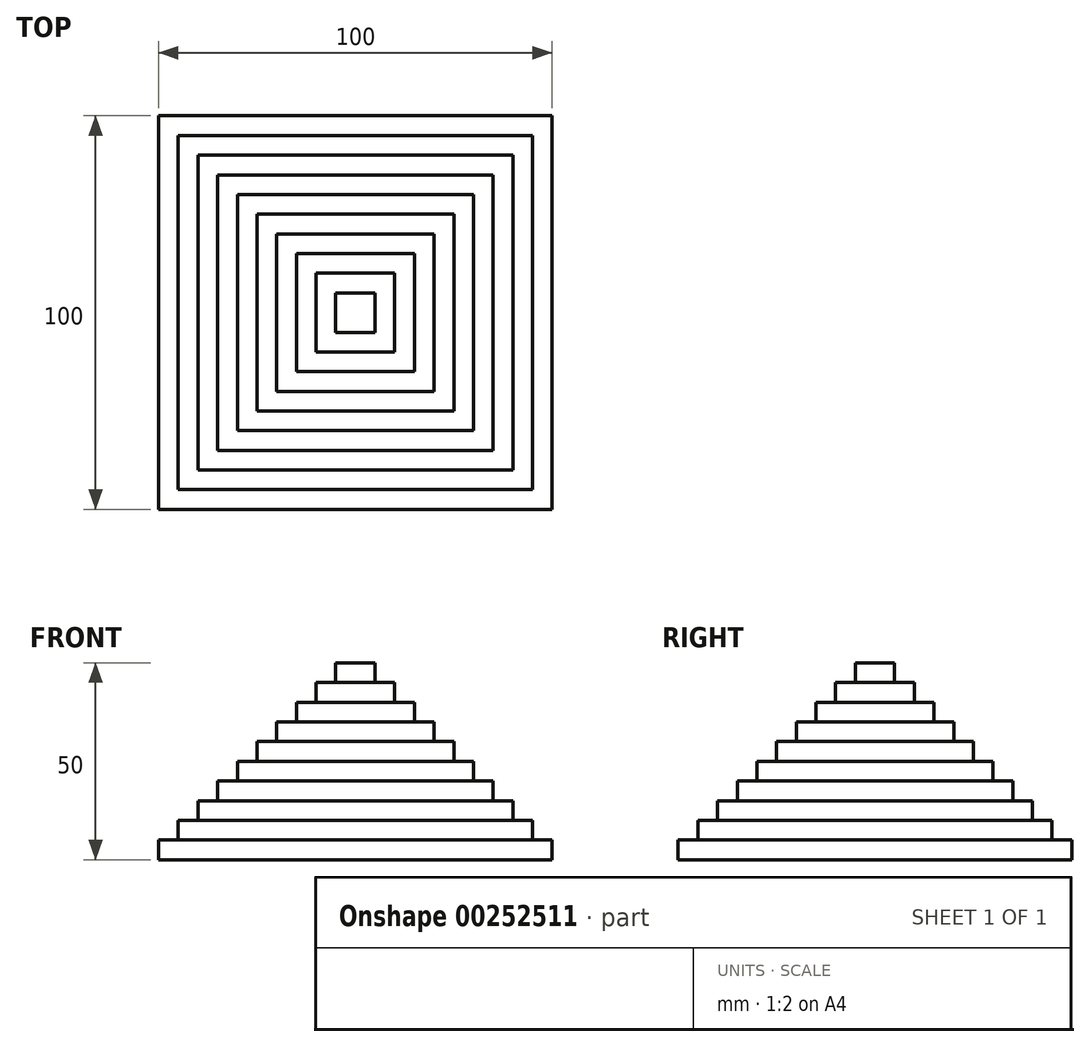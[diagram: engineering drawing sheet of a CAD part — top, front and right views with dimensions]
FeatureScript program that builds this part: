
annotation { "Feature Type Name" : "Feature", "Feature Type Description" : "" }
export const myFeature = defineFeature(function(context is Context, id is Id, definition is map)
    precondition{}
    {
        {
            var Q0;
            Q0=qCreatedBy(makeId("Top.planeOp"),FACE);
            var sketch = newSketch(context, id + "F0", { "sketchPlane" : qUnion([Q0])});
            skLineSegment(sketch, "E0.bottom", {"start": v(50, -50) * mm, "end": v(-50, -50) * mm});
            skLineSegment(sketch, "E0.top", {"start": v(50, 50) * mm, "end": v(-50, 50) * mm});
            skLineSegment(sketch, "E0.left", {"start": v(50, -50) * mm, "end": v(50, 50) * mm});
            skLineSegment(sketch, "E0.right", {"start": v(-50, -50) * mm, "end": v(-50, 50) * mm});
            skPoint(sketch, "E0.middle", {"position": v(0, 0) * mm});
            skSolve(sketch);
        }
        {
            var Q0;
            Q0 = qSketchRegion(id + "F0", true);
            extrude(context, id + "F1", {"entities" : qUnion([Q0]), "depth" : 5 * mm});
        }
        {
            var Q0;
            Q0=makeQuery(id+"F1.opExtrude","CAP_FACE",FACE,{"disambiguationData":[OSD([sQuery(id+"F0.wireOp",EDGE,"E0.bottom"),sQuery(id+"F0.wireOp",EDGE,"E0.top"),sQuery(id+"F0.wireOp",EDGE,"E0.left"),sQuery(id+"F0.wireOp",EDGE,"E0.right")])],"isStart":false});
            var sketch = newSketch(context, id + "F2", { "sketchPlane" : qUnion([Q0])});
            skLineSegment(sketch, "E1.bottom", {"start": v(47.5, -47.5) * mm, "end": v(-47.5, -47.5) * mm});
            skLineSegment(sketch, "E1.top", {"start": v(47.5, 47.5) * mm, "end": v(-47.5, 47.5) * mm});
            skLineSegment(sketch, "E1.left", {"start": v(47.5, -47.5) * mm, "end": v(47.5, 47.5) * mm});
            skLineSegment(sketch, "E1.right", {"start": v(-47.5, -47.5) * mm, "end": v(-47.5, 47.5) * mm});
            skPoint(sketch, "E1.middle", {"position": v(0, 0) * mm});
            skSolve(sketch);
        }
        {
            var Q0;
            Q0=makeQuery(id+"F2.imprint","IMPRINT",FACE,{"disambiguationData":[TD([[makeQuery(id+"F2.imprint","IMPRINT",EDGE,{"derivedFrom":sQuery(id+"F2.wireOp",EDGE,"E1.bottom")}),-1.0]])]});
            extrude(context, id + "F3", {"entities" : qUnion([Q0]), "operationType" : NewBodyOperationType.REMOVE, "oppositeDirection" : true, "depth" : 3 * mm});
        }
        {
            var Q0;
            Q0=makeQuery(id+"F3.boolean.opBoolean","COPY",FACE,{"derivedFrom":makeQuery(id+"F3.opExtrude","CAP_FACE",FACE,{"disambiguationData":[OSD([sQuery(id+"F2.wireOp",EDGE,"E1.bottom"),sQuery(id+"F2.wireOp",EDGE,"E1.top"),sQuery(id+"F2.wireOp",EDGE,"E1.left"),sQuery(id+"F2.wireOp",EDGE,"E1.right")])],"isStart":false})});
            var sketch = newSketch(context, id + "F4", { "sketchPlane" : qUnion([Q0])});
            skLineSegment(sketch, "E2.bottom", {"start": v(47.5, -47.5) * mm, "end": v(-47.5, -47.5) * mm});
            skLineSegment(sketch, "E2.top", {"start": v(47.5, 47.5) * mm, "end": v(-47.5, 47.5) * mm});
            skLineSegment(sketch, "E2.left", {"start": v(47.5, -47.5) * mm, "end": v(47.5, 47.5) * mm});
            skLineSegment(sketch, "E2.right", {"start": v(-47.5, -47.5) * mm, "end": v(-47.5, 47.5) * mm});
            skPoint(sketch, "E2.middle", {"position": v(0, 0) * mm});
            skSolve(sketch);
        }
        {
            var Q0;
            Q0 = qSketchRegion(id + "F4", true);
            extrude(context, id + "F5", {"entities" : qUnion([Q0]), "depth" : 2 * mm});
        }
        {
            var Q0;
            Q0=makeQuery(id+"F5.opExtrude","CAP_FACE",FACE,{"disambiguationData":[OSD([sQuery(id+"F4.wireOp",EDGE,"E2.bottom"),sQuery(id+"F4.wireOp",EDGE,"E2.top"),sQuery(id+"F4.wireOp",EDGE,"E2.left"),sQuery(id+"F4.wireOp",EDGE,"E2.right")])],"isStart":false});
            var sketch = newSketch(context, id + "F6", { "sketchPlane" : qUnion([Q0])});
            skLineSegment(sketch, "E3.bottom", {"start": v(47.5, -47.5) * mm, "end": v(-47.5, -47.5) * mm});
            skLineSegment(sketch, "E3.top", {"start": v(47.5, 47.5) * mm, "end": v(-47.5, 47.5) * mm});
            skLineSegment(sketch, "E3.left", {"start": v(47.5, -47.5) * mm, "end": v(47.5, 47.5) * mm});
            skLineSegment(sketch, "E3.right", {"start": v(-47.5, -47.5) * mm, "end": v(-47.5, 47.5) * mm});
            skPoint(sketch, "E3.middle", {"position": v(0, 0) * mm});
            skSolve(sketch);
        }
        {
            var Q0;
            Q0 = qSketchRegion(id + "F6", true);
            extrude(context, id + "F7", {"entities" : qUnion([Q0]), "operationType" : NewBodyOperationType.ADD, "depth" : 1 * mm});
        }
        {
            var Q0;
            Q0=makeQuery(id+"F7.boolean.opBoolean","MERGE",FACE,{"derivedFrom":[makeQuery(id+"F1.opExtrude","CAP_FACE",FACE,{"disambiguationData":[OSD([sQuery(id+"F0.wireOp",EDGE,"E0.bottom"),sQuery(id+"F0.wireOp",EDGE,"E0.top"),sQuery(id+"F0.wireOp",EDGE,"E0.left"),sQuery(id+"F0.wireOp",EDGE,"E0.right")])],"isStart":false}),makeQuery(id+"F7.opExtrude","CAP_FACE",FACE,{"disambiguationData":[OSD([sQuery(id+"F6.wireOp",EDGE,"E3.bottom"),sQuery(id+"F6.wireOp",EDGE,"E3.top"),sQuery(id+"F6.wireOp",EDGE,"E3.left"),sQuery(id+"F6.wireOp",EDGE,"E3.right")])],"isStart":false})]});
            var sketch = newSketch(context, id + "F8", { "sketchPlane" : qUnion([Q0])});
            skLineSegment(sketch, "E4.bottom", {"start": v(45, -45) * mm, "end": v(-45, -45) * mm});
            skLineSegment(sketch, "E4.top", {"start": v(45, 45) * mm, "end": v(-45, 45) * mm});
            skLineSegment(sketch, "E4.left", {"start": v(45, -45) * mm, "end": v(45, 45) * mm});
            skLineSegment(sketch, "E4.right", {"start": v(-45, -45) * mm, "end": v(-45, 45) * mm});
            skPoint(sketch, "E4.middle", {"position": v(0, 0) * mm});
            skSolve(sketch);
        }
        {
            var Q0;
            Q0 = qSketchRegion(id + "F8", true);
            extrude(context, id + "F9", {"entities" : qUnion([Q0]), "operationType" : NewBodyOperationType.ADD, "depth" : 5 * mm});
        }
        {
            var Q0;
            Q0=makeQuery(id+"F9.opExtrude","CAP_FACE",FACE,{"disambiguationData":[OSD([sQuery(id+"F8.wireOp",EDGE,"E4.bottom"),sQuery(id+"F8.wireOp",EDGE,"E4.top"),sQuery(id+"F8.wireOp",EDGE,"E4.left"),sQuery(id+"F8.wireOp",EDGE,"E4.right")])],"isStart":false});
            var sketch = newSketch(context, id + "F10", { "sketchPlane" : qUnion([Q0])});
            skLineSegment(sketch, "E5.bottom", {"start": v(42.5, -42.5) * mm, "end": v(-42.5, -42.5) * mm});
            skLineSegment(sketch, "E5.top", {"start": v(42.5, 42.5) * mm, "end": v(-42.5, 42.5) * mm});
            skLineSegment(sketch, "E5.left", {"start": v(42.5, -42.5) * mm, "end": v(42.5, 42.5) * mm});
            skLineSegment(sketch, "E5.right", {"start": v(-42.5, -42.5) * mm, "end": v(-42.5, 42.5) * mm});
            skPoint(sketch, "E5.middle", {"position": v(0, 0) * mm});
            skSolve(sketch);
        }
        {
            var Q0;
            Q0 = qSketchRegion(id + "F10", true);
            extrude(context, id + "F11", {"entities" : qUnion([Q0]), "operationType" : NewBodyOperationType.REMOVE, "oppositeDirection" : true, "depth" : 3 * mm});
        }
        {
            var Q0;
            Q0=makeQuery(id+"F11.boolean.opBoolean","COPY",FACE,{"derivedFrom":makeQuery(id+"F11.opExtrude","CAP_FACE",FACE,{"disambiguationData":[OSD([sQuery(id+"F10.wireOp",EDGE,"E5.bottom"),sQuery(id+"F10.wireOp",EDGE,"E5.top"),sQuery(id+"F10.wireOp",EDGE,"E5.left"),sQuery(id+"F10.wireOp",EDGE,"E5.right")])],"isStart":false})});
            var sketch = newSketch(context, id + "F12", { "sketchPlane" : qUnion([Q0])});
            skLineSegment(sketch, "E6.bottom", {"start": v(42.5, -42.5) * mm, "end": v(-42.5, -42.5) * mm});
            skLineSegment(sketch, "E6.top", {"start": v(42.5, 42.5) * mm, "end": v(-42.5, 42.5) * mm});
            skLineSegment(sketch, "E6.left", {"start": v(42.5, -42.5) * mm, "end": v(42.5, 42.5) * mm});
            skLineSegment(sketch, "E6.right", {"start": v(-42.5, -42.5) * mm, "end": v(-42.5, 42.5) * mm});
            skPoint(sketch, "E6.middle", {"position": v(0, 0) * mm});
            skSolve(sketch);
        }
        {
            var Q0;
            Q0 = qSketchRegion(id + "F12", true);
            extrude(context, id + "F13", {"entities" : qUnion([Q0]), "depth" : 2 * mm});
        }
        {
            var Q0;
            Q0=makeQuery(id+"F13.opExtrude","CAP_FACE",FACE,{"disambiguationData":[OSD([sQuery(id+"F12.wireOp",EDGE,"E6.bottom"),sQuery(id+"F12.wireOp",EDGE,"E6.top"),sQuery(id+"F12.wireOp",EDGE,"E6.left"),sQuery(id+"F12.wireOp",EDGE,"E6.right")])],"isStart":false});
            var sketch = newSketch(context, id + "F14", { "sketchPlane" : qUnion([Q0])});
            skLineSegment(sketch, "E7.bottom", {"start": v(42.5, -42.5) * mm, "end": v(-42.5, -42.5) * mm});
            skLineSegment(sketch, "E7.top", {"start": v(42.5, 42.5) * mm, "end": v(-42.5, 42.5) * mm});
            skLineSegment(sketch, "E7.left", {"start": v(42.5, -42.5) * mm, "end": v(42.5, 42.5) * mm});
            skLineSegment(sketch, "E7.right", {"start": v(-42.5, -42.5) * mm, "end": v(-42.5, 42.5) * mm});
            skPoint(sketch, "E7.middle", {"position": v(0, 0) * mm});
            skSolve(sketch);
        }
        {
            var Q0;
            Q0 = qSketchRegion(id + "F14", true);
            extrude(context, id + "F15", {"entities" : qUnion([Q0]), "operationType" : NewBodyOperationType.ADD, "depth" : 1 * mm});
        }
        {
            var Q0;
            Q0=makeQuery(id+"F15.boolean.opBoolean","MERGE",FACE,{"derivedFrom":[makeQuery(id+"F9.opExtrude","CAP_FACE",FACE,{"disambiguationData":[OSD([sQuery(id+"F8.wireOp",EDGE,"E4.bottom"),sQuery(id+"F8.wireOp",EDGE,"E4.top"),sQuery(id+"F8.wireOp",EDGE,"E4.left"),sQuery(id+"F8.wireOp",EDGE,"E4.right")])],"isStart":false}),makeQuery(id+"F15.opExtrude","CAP_FACE",FACE,{"disambiguationData":[OSD([sQuery(id+"F14.wireOp",EDGE,"E7.bottom"),sQuery(id+"F14.wireOp",EDGE,"E7.top"),sQuery(id+"F14.wireOp",EDGE,"E7.left"),sQuery(id+"F14.wireOp",EDGE,"E7.right")])],"isStart":false})]});
            var sketch = newSketch(context, id + "F16", { "sketchPlane" : qUnion([Q0])});
            skLineSegment(sketch, "E8.bottom", {"start": v(40, -40) * mm, "end": v(-40, -40) * mm});
            skLineSegment(sketch, "E8.top", {"start": v(40, 40) * mm, "end": v(-40, 40) * mm});
            skLineSegment(sketch, "E8.left", {"start": v(40, -40) * mm, "end": v(40, 40) * mm});
            skLineSegment(sketch, "E8.right", {"start": v(-40, -40) * mm, "end": v(-40, 40) * mm});
            skPoint(sketch, "E8.middle", {"position": v(0, 0) * mm});
            skSolve(sketch);
        }
        {
            var Q0;
            Q0 = qSketchRegion(id + "F16", true);
            extrude(context, id + "F17", {"entities" : qUnion([Q0]), "operationType" : NewBodyOperationType.ADD, "depth" : 5 * mm});
        }
        {
            var Q0;
            Q0=makeQuery(id+"F17.opExtrude","CAP_FACE",FACE,{"disambiguationData":[OSD([sQuery(id+"F16.wireOp",EDGE,"E8.bottom"),sQuery(id+"F16.wireOp",EDGE,"E8.top"),sQuery(id+"F16.wireOp",EDGE,"E8.left"),sQuery(id+"F16.wireOp",EDGE,"E8.right")])],"isStart":false});
            var sketch = newSketch(context, id + "F18", { "sketchPlane" : qUnion([Q0])});
            skLineSegment(sketch, "E9.bottom", {"start": v(37.5, -37.5) * mm, "end": v(-37.5, -37.5) * mm});
            skLineSegment(sketch, "E9.top", {"start": v(37.5, 37.5) * mm, "end": v(-37.5, 37.5) * mm});
            skLineSegment(sketch, "E9.left", {"start": v(37.5, -37.5) * mm, "end": v(37.5, 37.5) * mm});
            skLineSegment(sketch, "E9.right", {"start": v(-37.5, -37.5) * mm, "end": v(-37.5, 37.5) * mm});
            skPoint(sketch, "E9.middle", {"position": v(0, 0) * mm});
            skSolve(sketch);
        }
        {
            var Q0;
            Q0 = qSketchRegion(id + "F18", true);
            extrude(context, id + "F19", {"entities" : qUnion([Q0]), "operationType" : NewBodyOperationType.REMOVE, "oppositeDirection" : true, "depth" : 3 * mm});
        }
        {
            var Q0;
            Q0=makeQuery(id+"F19.boolean.opBoolean","COPY",FACE,{"derivedFrom":makeQuery(id+"F19.opExtrude","CAP_FACE",FACE,{"disambiguationData":[OSD([sQuery(id+"F18.wireOp",EDGE,"E9.bottom"),sQuery(id+"F18.wireOp",EDGE,"E9.top"),sQuery(id+"F18.wireOp",EDGE,"E9.left"),sQuery(id+"F18.wireOp",EDGE,"E9.right")])],"isStart":false})});
            var sketch = newSketch(context, id + "F20", { "sketchPlane" : qUnion([Q0])});
            skLineSegment(sketch, "E10.bottom", {"start": v(37.5, -37.5) * mm, "end": v(-37.5, -37.5) * mm});
            skLineSegment(sketch, "E10.top", {"start": v(37.5, 37.5) * mm, "end": v(-37.5, 37.5) * mm});
            skLineSegment(sketch, "E10.left", {"start": v(37.5, -37.5) * mm, "end": v(37.5, 37.5) * mm});
            skLineSegment(sketch, "E10.right", {"start": v(-37.5, -37.5) * mm, "end": v(-37.5, 37.5) * mm});
            skPoint(sketch, "E10.middle", {"position": v(0, 0) * mm});
            skSolve(sketch);
        }
        {
            var Q0;
            Q0 = qSketchRegion(id + "F20", true);
            extrude(context, id + "F21", {"entities" : qUnion([Q0]), "depth" : 2 * mm});
        }
        {
            var Q0;
            Q0=makeQuery(id+"F21.opExtrude","CAP_FACE",FACE,{"disambiguationData":[OSD([sQuery(id+"F20.wireOp",EDGE,"E10.bottom"),sQuery(id+"F20.wireOp",EDGE,"E10.top"),sQuery(id+"F20.wireOp",EDGE,"E10.left"),sQuery(id+"F20.wireOp",EDGE,"E10.right")])],"isStart":false});
            var sketch = newSketch(context, id + "F22", { "sketchPlane" : qUnion([Q0])});
            skLineSegment(sketch, "E11.bottom", {"start": v(37.5, -37.5) * mm, "end": v(-37.5, -37.5) * mm});
            skLineSegment(sketch, "E11.top", {"start": v(37.5, 37.5) * mm, "end": v(-37.5, 37.5) * mm});
            skLineSegment(sketch, "E11.left", {"start": v(37.5, -37.5) * mm, "end": v(37.5, 37.5) * mm});
            skLineSegment(sketch, "E11.right", {"start": v(-37.5, -37.5) * mm, "end": v(-37.5, 37.5) * mm});
            skPoint(sketch, "E11.middle", {"position": v(0, 0) * mm});
            skSolve(sketch);
        }
        {
            var Q0;
            Q0 = qSketchRegion(id + "F22", true);
            extrude(context, id + "F23", {"entities" : qUnion([Q0]), "operationType" : NewBodyOperationType.ADD, "depth" : 1 * mm});
        }
        {
            var Q0;
            Q0=makeQuery(id+"F23.boolean.opBoolean","MERGE",FACE,{"derivedFrom":[makeQuery(id+"F17.opExtrude","CAP_FACE",FACE,{"disambiguationData":[OSD([sQuery(id+"F16.wireOp",EDGE,"E8.bottom"),sQuery(id+"F16.wireOp",EDGE,"E8.top"),sQuery(id+"F16.wireOp",EDGE,"E8.left"),sQuery(id+"F16.wireOp",EDGE,"E8.right")])],"isStart":false}),makeQuery(id+"F23.opExtrude","CAP_FACE",FACE,{"disambiguationData":[OSD([sQuery(id+"F22.wireOp",EDGE,"E11.bottom"),sQuery(id+"F22.wireOp",EDGE,"E11.top"),sQuery(id+"F22.wireOp",EDGE,"E11.left"),sQuery(id+"F22.wireOp",EDGE,"E11.right")])],"isStart":false})]});
            var sketch = newSketch(context, id + "F24", { "sketchPlane" : qUnion([Q0])});
            skLineSegment(sketch, "E12.bottom", {"start": v(35, -35) * mm, "end": v(-35, -35) * mm});
            skLineSegment(sketch, "E12.top", {"start": v(35, 35) * mm, "end": v(-35, 35) * mm});
            skLineSegment(sketch, "E12.left", {"start": v(35, -35) * mm, "end": v(35, 35) * mm});
            skLineSegment(sketch, "E12.right", {"start": v(-35, -35) * mm, "end": v(-35, 35) * mm});
            skPoint(sketch, "E12.middle", {"position": v(0, 0) * mm});
            skSolve(sketch);
        }
        {
            var Q0;
            Q0=makeQuery(id+"F24.imprint","IMPRINT",FACE,{"disambiguationData":[TD([[makeQuery(id+"F24.imprint","IMPRINT",EDGE,{"derivedFrom":sQuery(id+"F24.wireOp",EDGE,"E12.bottom")}),-1.0]])]});
            extrude(context, id + "F25", {"entities" : qUnion([Q0]), "operationType" : NewBodyOperationType.ADD, "depth" : 5 * mm});
        }
        {
            var Q0;
            Q0=makeQuery(id+"F25.opExtrude","CAP_FACE",FACE,{"disambiguationData":[OSD([sQuery(id+"F24.wireOp",EDGE,"E12.bottom"),sQuery(id+"F24.wireOp",EDGE,"E12.top"),sQuery(id+"F24.wireOp",EDGE,"E12.left"),sQuery(id+"F24.wireOp",EDGE,"E12.right")])],"isStart":false});
            var sketch = newSketch(context, id + "F26", { "sketchPlane" : qUnion([Q0])});
            skLineSegment(sketch, "E13.bottom", {"start": v(32.5, -32.5) * mm, "end": v(-32.5, -32.5) * mm});
            skLineSegment(sketch, "E13.top", {"start": v(32.5, 32.5) * mm, "end": v(-32.5, 32.5) * mm});
            skLineSegment(sketch, "E13.left", {"start": v(32.5, -32.5) * mm, "end": v(32.5, 32.5) * mm});
            skLineSegment(sketch, "E13.right", {"start": v(-32.5, -32.5) * mm, "end": v(-32.5, 32.5) * mm});
            skPoint(sketch, "E13.middle", {"position": v(0, 0) * mm});
            skSolve(sketch);
        }
        {
            var Q0;
            Q0 = qSketchRegion(id + "F26", true);
            extrude(context, id + "F27", {"entities" : qUnion([Q0]), "operationType" : NewBodyOperationType.REMOVE, "oppositeDirection" : true, "depth" : 3 * mm});
        }
        {
            var Q0;
            Q0=makeQuery(id+"F27.boolean.opBoolean","COPY",FACE,{"derivedFrom":makeQuery(id+"F27.opExtrude","CAP_FACE",FACE,{"disambiguationData":[OSD([sQuery(id+"F26.wireOp",EDGE,"E13.bottom"),sQuery(id+"F26.wireOp",EDGE,"E13.top"),sQuery(id+"F26.wireOp",EDGE,"E13.left"),sQuery(id+"F26.wireOp",EDGE,"E13.right")])],"isStart":false})});
            var sketch = newSketch(context, id + "F28", { "sketchPlane" : qUnion([Q0])});
            skLineSegment(sketch, "E14.bottom", {"start": v(32.5, -32.5) * mm, "end": v(-32.5, -32.5) * mm});
            skLineSegment(sketch, "E14.top", {"start": v(32.5, 32.5) * mm, "end": v(-32.5, 32.5) * mm});
            skLineSegment(sketch, "E14.left", {"start": v(32.5, -32.5) * mm, "end": v(32.5, 32.5) * mm});
            skLineSegment(sketch, "E14.right", {"start": v(-32.5, -32.5) * mm, "end": v(-32.5, 32.5) * mm});
            skPoint(sketch, "E14.middle", {"position": v(0, 0) * mm});
            skSolve(sketch);
        }
        {
            var Q0;
            Q0 = qSketchRegion(id + "F28", true);
            extrude(context, id + "F29", {"entities" : qUnion([Q0]), "depth" : 2 * mm});
        }
        {
            var Q0;
            Q0=makeQuery(id+"F29.opExtrude","CAP_FACE",FACE,{"disambiguationData":[OSD([sQuery(id+"F28.wireOp",EDGE,"E14.bottom"),sQuery(id+"F28.wireOp",EDGE,"E14.top"),sQuery(id+"F28.wireOp",EDGE,"E14.left"),sQuery(id+"F28.wireOp",EDGE,"E14.right")])],"isStart":false});
            var sketch = newSketch(context, id + "F30", { "sketchPlane" : qUnion([Q0])});
            skLineSegment(sketch, "E15.bottom", {"start": v(32.5, -32.5) * mm, "end": v(-32.5, -32.5) * mm});
            skLineSegment(sketch, "E15.top", {"start": v(32.5, 32.5) * mm, "end": v(-32.5, 32.5) * mm});
            skLineSegment(sketch, "E15.left", {"start": v(32.5, -32.5) * mm, "end": v(32.5, 32.5) * mm});
            skLineSegment(sketch, "E15.right", {"start": v(-32.5, -32.5) * mm, "end": v(-32.5, 32.5) * mm});
            skPoint(sketch, "E15.middle", {"position": v(0, 0) * mm});
            skSolve(sketch);
        }
        {
            var Q0;
            Q0 = qSketchRegion(id + "F30", true);
            extrude(context, id + "F31", {"entities" : qUnion([Q0]), "operationType" : NewBodyOperationType.ADD, "depth" : 1 * mm});
        }
        {
            var Q0;
            Q0=makeQuery(id+"F31.boolean.opBoolean","MERGE",FACE,{"derivedFrom":[makeQuery(id+"F25.opExtrude","CAP_FACE",FACE,{"disambiguationData":[OSD([sQuery(id+"F24.wireOp",EDGE,"E12.bottom"),sQuery(id+"F24.wireOp",EDGE,"E12.top"),sQuery(id+"F24.wireOp",EDGE,"E12.left"),sQuery(id+"F24.wireOp",EDGE,"E12.right")])],"isStart":false}),makeQuery(id+"F31.opExtrude","CAP_FACE",FACE,{"disambiguationData":[OSD([sQuery(id+"F30.wireOp",EDGE,"E15.bottom"),sQuery(id+"F30.wireOp",EDGE,"E15.top"),sQuery(id+"F30.wireOp",EDGE,"E15.left"),sQuery(id+"F30.wireOp",EDGE,"E15.right")])],"isStart":false})]});
            var sketch = newSketch(context, id + "F32", { "sketchPlane" : qUnion([Q0])});
            skLineSegment(sketch, "E16.bottom", {"start": v(30, -30) * mm, "end": v(-30, -30) * mm});
            skLineSegment(sketch, "E16.top", {"start": v(30, 30) * mm, "end": v(-30, 30) * mm});
            skLineSegment(sketch, "E16.left", {"start": v(30, -30) * mm, "end": v(30, 30) * mm});
            skLineSegment(sketch, "E16.right", {"start": v(-30, -30) * mm, "end": v(-30, 30) * mm});
            skPoint(sketch, "E16.middle", {"position": v(0, 0) * mm});
            skSolve(sketch);
        }
        {
            var Q0;
            Q0 = qSketchRegion(id + "F32", true);
            extrude(context, id + "F33", {"entities" : qUnion([Q0]), "operationType" : NewBodyOperationType.ADD, "depth" : 5 * mm});
        }
        {
            var Q0;
            Q0=makeQuery(id+"F33.opExtrude","CAP_FACE",FACE,{"disambiguationData":[OSD([sQuery(id+"F32.wireOp",EDGE,"E16.bottom"),sQuery(id+"F32.wireOp",EDGE,"E16.top"),sQuery(id+"F32.wireOp",EDGE,"E16.left"),sQuery(id+"F32.wireOp",EDGE,"E16.right")])],"isStart":false});
            var sketch = newSketch(context, id + "F34", { "sketchPlane" : qUnion([Q0])});
            skLineSegment(sketch, "E17.bottom", {"start": v(27.5, -27.5) * mm, "end": v(-27.5, -27.5) * mm});
            skLineSegment(sketch, "E17.top", {"start": v(27.5, 27.5) * mm, "end": v(-27.5, 27.5) * mm});
            skLineSegment(sketch, "E17.left", {"start": v(27.5, -27.5) * mm, "end": v(27.5, 27.5) * mm});
            skLineSegment(sketch, "E17.right", {"start": v(-27.5, -27.5) * mm, "end": v(-27.5, 27.5) * mm});
            skPoint(sketch, "E17.middle", {"position": v(0, 0) * mm});
            skSolve(sketch);
        }
        {
            var Q0;
            Q0 = qSketchRegion(id + "F34", true);
            extrude(context, id + "F35", {"entities" : qUnion([Q0]), "operationType" : NewBodyOperationType.REMOVE, "oppositeDirection" : true, "depth" : 3 * mm});
        }
        {
            var Q0;
            Q0=makeQuery(id+"F35.boolean.opBoolean","COPY",FACE,{"derivedFrom":makeQuery(id+"F35.opExtrude","CAP_FACE",FACE,{"disambiguationData":[OSD([sQuery(id+"F34.wireOp",EDGE,"E17.bottom"),sQuery(id+"F34.wireOp",EDGE,"E17.top"),sQuery(id+"F34.wireOp",EDGE,"E17.left"),sQuery(id+"F34.wireOp",EDGE,"E17.right")])],"isStart":false})});
            var sketch = newSketch(context, id + "F36", { "sketchPlane" : qUnion([Q0])});
            skLineSegment(sketch, "E18.bottom", {"start": v(27.5, -27.5) * mm, "end": v(-27.5, -27.5) * mm});
            skLineSegment(sketch, "E18.top", {"start": v(27.5, 27.5) * mm, "end": v(-27.5, 27.5) * mm});
            skLineSegment(sketch, "E18.left", {"start": v(27.5, -27.5) * mm, "end": v(27.5, 27.5) * mm});
            skLineSegment(sketch, "E18.right", {"start": v(-27.5, -27.5) * mm, "end": v(-27.5, 27.5) * mm});
            skPoint(sketch, "E18.middle", {"position": v(0, 0) * mm});
            skSolve(sketch);
        }
        {
            var Q0;
            Q0 = qSketchRegion(id + "F36", true);
            extrude(context, id + "F37", {"entities" : qUnion([Q0]), "depth" : 2 * mm});
        }
        {
            var Q0;
            Q0=makeQuery(id+"F37.opExtrude","CAP_FACE",FACE,{"disambiguationData":[OSD([sQuery(id+"F36.wireOp",EDGE,"E18.bottom"),sQuery(id+"F36.wireOp",EDGE,"E18.top"),sQuery(id+"F36.wireOp",EDGE,"E18.left"),sQuery(id+"F36.wireOp",EDGE,"E18.right")])],"isStart":false});
            var sketch = newSketch(context, id + "F38", { "sketchPlane" : qUnion([Q0])});
            skLineSegment(sketch, "E19.bottom", {"start": v(27.5, -27.5) * mm, "end": v(-27.5, -27.5) * mm});
            skLineSegment(sketch, "E19.top", {"start": v(27.5, 27.5) * mm, "end": v(-27.5, 27.5) * mm});
            skLineSegment(sketch, "E19.left", {"start": v(27.5, -27.5) * mm, "end": v(27.5, 27.5) * mm});
            skLineSegment(sketch, "E19.right", {"start": v(-27.5, -27.5) * mm, "end": v(-27.5, 27.5) * mm});
            skPoint(sketch, "E19.middle", {"position": v(0, 0) * mm});
            skSolve(sketch);
        }
        {
            var Q0;
            Q0 = qSketchRegion(id + "F38", true);
            extrude(context, id + "F39", {"entities" : qUnion([Q0]), "operationType" : NewBodyOperationType.ADD, "depth" : 1 * mm});
        }
        {
            var Q0;
            Q0=makeQuery(id+"F39.boolean.opBoolean","MERGE",FACE,{"derivedFrom":[makeQuery(id+"F33.opExtrude","CAP_FACE",FACE,{"disambiguationData":[OSD([sQuery(id+"F32.wireOp",EDGE,"E16.bottom"),sQuery(id+"F32.wireOp",EDGE,"E16.top"),sQuery(id+"F32.wireOp",EDGE,"E16.left"),sQuery(id+"F32.wireOp",EDGE,"E16.right")])],"isStart":false}),makeQuery(id+"F39.opExtrude","CAP_FACE",FACE,{"disambiguationData":[OSD([sQuery(id+"F38.wireOp",EDGE,"E19.bottom"),sQuery(id+"F38.wireOp",EDGE,"E19.top"),sQuery(id+"F38.wireOp",EDGE,"E19.left"),sQuery(id+"F38.wireOp",EDGE,"E19.right")])],"isStart":false})]});
            var sketch = newSketch(context, id + "F40", { "sketchPlane" : qUnion([Q0])});
            skLineSegment(sketch, "E20.bottom", {"start": v(25, -25) * mm, "end": v(-25, -25) * mm});
            skLineSegment(sketch, "E20.top", {"start": v(25, 25) * mm, "end": v(-25, 25) * mm});
            skLineSegment(sketch, "E20.left", {"start": v(25, -25) * mm, "end": v(25, 25) * mm});
            skLineSegment(sketch, "E20.right", {"start": v(-25, -25) * mm, "end": v(-25, 25) * mm});
            skPoint(sketch, "E20.middle", {"position": v(0, 0) * mm});
            skSolve(sketch);
        }
        {
            var Q0;
            Q0 = qSketchRegion(id + "F40", true);
            extrude(context, id + "F41", {"entities" : qUnion([Q0]), "operationType" : NewBodyOperationType.ADD, "depth" : 5 * mm});
        }
        {
            var Q0;
            Q0=makeQuery(id+"F41.opExtrude","CAP_FACE",FACE,{"disambiguationData":[OSD([sQuery(id+"F40.wireOp",EDGE,"E20.bottom"),sQuery(id+"F40.wireOp",EDGE,"E20.top"),sQuery(id+"F40.wireOp",EDGE,"E20.left"),sQuery(id+"F40.wireOp",EDGE,"E20.right")])],"isStart":false});
            var sketch = newSketch(context, id + "F42", { "sketchPlane" : qUnion([Q0])});
            skLineSegment(sketch, "E21.bottom", {"start": v(22.5, -22.5) * mm, "end": v(-22.5, -22.5) * mm});
            skLineSegment(sketch, "E21.top", {"start": v(22.5, 22.5) * mm, "end": v(-22.5, 22.5) * mm});
            skLineSegment(sketch, "E21.left", {"start": v(22.5, -22.5) * mm, "end": v(22.5, 22.5) * mm});
            skLineSegment(sketch, "E21.right", {"start": v(-22.5, -22.5) * mm, "end": v(-22.5, 22.5) * mm});
            skPoint(sketch, "E21.middle", {"position": v(0, 0) * mm});
            skSolve(sketch);
        }
        {
            var Q0;
            Q0 = qSketchRegion(id + "F42", true);
            extrude(context, id + "F43", {"entities" : qUnion([Q0]), "operationType" : NewBodyOperationType.REMOVE, "oppositeDirection" : true, "depth" : 3 * mm});
        }
        {
            var Q0;
            Q0=makeQuery(id+"F43.boolean.opBoolean","COPY",FACE,{"derivedFrom":makeQuery(id+"F43.opExtrude","CAP_FACE",FACE,{"disambiguationData":[OSD([sQuery(id+"F42.wireOp",EDGE,"E21.bottom"),sQuery(id+"F42.wireOp",EDGE,"E21.top"),sQuery(id+"F42.wireOp",EDGE,"E21.left"),sQuery(id+"F42.wireOp",EDGE,"E21.right")])],"isStart":false})});
            var sketch = newSketch(context, id + "F44", { "sketchPlane" : qUnion([Q0])});
            skLineSegment(sketch, "E22.bottom", {"start": v(22.5, -22.5) * mm, "end": v(-22.5, -22.5) * mm});
            skLineSegment(sketch, "E22.top", {"start": v(22.5, 22.5) * mm, "end": v(-22.5, 22.5) * mm});
            skLineSegment(sketch, "E22.left", {"start": v(22.5, -22.5) * mm, "end": v(22.5, 22.5) * mm});
            skLineSegment(sketch, "E22.right", {"start": v(-22.5, -22.5) * mm, "end": v(-22.5, 22.5) * mm});
            skPoint(sketch, "E22.middle", {"position": v(0, 0) * mm});
            skSolve(sketch);
        }
        {
            var Q0;
            Q0 = qSketchRegion(id + "F44", true);
            extrude(context, id + "F45", {"entities" : qUnion([Q0]), "depth" : 2 * mm});
        }
        {
            var Q0;
            Q0=makeQuery(id+"F45.opExtrude","CAP_FACE",FACE,{"disambiguationData":[OSD([sQuery(id+"F44.wireOp",EDGE,"E22.bottom"),sQuery(id+"F44.wireOp",EDGE,"E22.top"),sQuery(id+"F44.wireOp",EDGE,"E22.left"),sQuery(id+"F44.wireOp",EDGE,"E22.right")])],"isStart":false});
            var sketch = newSketch(context, id + "F46", { "sketchPlane" : qUnion([Q0])});
            skLineSegment(sketch, "E23.bottom", {"start": v(22.5, -22.5) * mm, "end": v(-22.5, -22.5) * mm});
            skLineSegment(sketch, "E23.top", {"start": v(22.5, 22.5) * mm, "end": v(-22.5, 22.5) * mm});
            skLineSegment(sketch, "E23.left", {"start": v(22.5, -22.5) * mm, "end": v(22.5, 22.5) * mm});
            skLineSegment(sketch, "E23.right", {"start": v(-22.5, -22.5) * mm, "end": v(-22.5, 22.5) * mm});
            skPoint(sketch, "E23.middle", {"position": v(0, 0) * mm});
            skSolve(sketch);
        }
        {
            var Q0;
            Q0 = qSketchRegion(id + "F46", true);
            extrude(context, id + "F47", {"entities" : qUnion([Q0]), "operationType" : NewBodyOperationType.ADD, "depth" : 1 * mm});
        }
        {
            var Q0;
            Q0=makeQuery(id+"F47.boolean.opBoolean","MERGE",FACE,{"derivedFrom":[makeQuery(id+"F41.opExtrude","CAP_FACE",FACE,{"disambiguationData":[OSD([sQuery(id+"F40.wireOp",EDGE,"E20.bottom"),sQuery(id+"F40.wireOp",EDGE,"E20.top"),sQuery(id+"F40.wireOp",EDGE,"E20.left"),sQuery(id+"F40.wireOp",EDGE,"E20.right")])],"isStart":false}),makeQuery(id+"F47.opExtrude","CAP_FACE",FACE,{"disambiguationData":[OSD([sQuery(id+"F46.wireOp",EDGE,"E23.bottom"),sQuery(id+"F46.wireOp",EDGE,"E23.top"),sQuery(id+"F46.wireOp",EDGE,"E23.left"),sQuery(id+"F46.wireOp",EDGE,"E23.right")])],"isStart":false})]});
            var sketch = newSketch(context, id + "F48", { "sketchPlane" : qUnion([Q0])});
            skLineSegment(sketch, "E24.bottom", {"start": v(20, -20) * mm, "end": v(-20, -20) * mm});
            skLineSegment(sketch, "E24.top", {"start": v(20, 20) * mm, "end": v(-20, 20) * mm});
            skLineSegment(sketch, "E24.left", {"start": v(20, -20) * mm, "end": v(20, 20) * mm});
            skLineSegment(sketch, "E24.right", {"start": v(-20, -20) * mm, "end": v(-20, 20) * mm});
            skPoint(sketch, "E24.middle", {"position": v(0, 0) * mm});
            skSolve(sketch);
        }
        {
            var Q0;
            Q0 = qSketchRegion(id + "F48", true);
            extrude(context, id + "F49", {"entities" : qUnion([Q0]), "operationType" : NewBodyOperationType.ADD, "depth" : 5 * mm});
        }
        {
            var Q0;
            Q0=makeQuery(id+"F49.opExtrude","CAP_FACE",FACE,{"disambiguationData":[OSD([sQuery(id+"F48.wireOp",EDGE,"E24.bottom"),sQuery(id+"F48.wireOp",EDGE,"E24.top"),sQuery(id+"F48.wireOp",EDGE,"E24.left"),sQuery(id+"F48.wireOp",EDGE,"E24.right")])],"isStart":false});
            var sketch = newSketch(context, id + "F50", { "sketchPlane" : qUnion([Q0])});
            skLineSegment(sketch, "E25.bottom", {"start": v(17.5, -17.5) * mm, "end": v(-17.5, -17.5) * mm});
            skLineSegment(sketch, "E25.top", {"start": v(17.5, 17.5) * mm, "end": v(-17.5, 17.5) * mm});
            skLineSegment(sketch, "E25.left", {"start": v(17.5, -17.5) * mm, "end": v(17.5, 17.5) * mm});
            skLineSegment(sketch, "E25.right", {"start": v(-17.5, -17.5) * mm, "end": v(-17.5, 17.5) * mm});
            skPoint(sketch, "E25.middle", {"position": v(0, 0) * mm});
            skSolve(sketch);
        }
        {
            var Q0;
            Q0 = qSketchRegion(id + "F50", true);
            extrude(context, id + "F51", {"entities" : qUnion([Q0]), "operationType" : NewBodyOperationType.REMOVE, "oppositeDirection" : true, "depth" : 3 * mm});
        }
        {
            var Q0;
            Q0=makeQuery(id+"F51.boolean.opBoolean","COPY",FACE,{"derivedFrom":makeQuery(id+"F51.opExtrude","CAP_FACE",FACE,{"disambiguationData":[OSD([sQuery(id+"F50.wireOp",EDGE,"E25.bottom"),sQuery(id+"F50.wireOp",EDGE,"E25.top"),sQuery(id+"F50.wireOp",EDGE,"E25.left"),sQuery(id+"F50.wireOp",EDGE,"E25.right")])],"isStart":false})});
            var sketch = newSketch(context, id + "F52", { "sketchPlane" : qUnion([Q0])});
            skLineSegment(sketch, "E26.bottom", {"start": v(17.5, -17.5) * mm, "end": v(-17.5, -17.5) * mm});
            skLineSegment(sketch, "E26.top", {"start": v(17.5, 17.5) * mm, "end": v(-17.5, 17.5) * mm});
            skLineSegment(sketch, "E26.left", {"start": v(17.5, -17.5) * mm, "end": v(17.5, 17.5) * mm});
            skLineSegment(sketch, "E26.right", {"start": v(-17.5, -17.5) * mm, "end": v(-17.5, 17.5) * mm});
            skPoint(sketch, "E26.middle", {"position": v(0, 0) * mm});
            skSolve(sketch);
        }
        {
            var Q0;
            Q0 = qSketchRegion(id + "F52", true);
            extrude(context, id + "F53", {"entities" : qUnion([Q0]), "depth" : 2 * mm});
        }
        {
            var Q0;
            Q0=makeQuery(id+"F53.opExtrude","CAP_FACE",FACE,{"disambiguationData":[OSD([sQuery(id+"F52.wireOp",EDGE,"E26.bottom"),sQuery(id+"F52.wireOp",EDGE,"E26.top"),sQuery(id+"F52.wireOp",EDGE,"E26.left"),sQuery(id+"F52.wireOp",EDGE,"E26.right")])],"isStart":false});
            var sketch = newSketch(context, id + "F54", { "sketchPlane" : qUnion([Q0])});
            skLineSegment(sketch, "E27.bottom", {"start": v(17.5, -17.5) * mm, "end": v(-17.5, -17.5) * mm});
            skLineSegment(sketch, "E27.top", {"start": v(17.5, 17.5) * mm, "end": v(-17.5, 17.5) * mm});
            skLineSegment(sketch, "E27.left", {"start": v(17.5, -17.5) * mm, "end": v(17.5, 17.5) * mm});
            skLineSegment(sketch, "E27.right", {"start": v(-17.5, -17.5) * mm, "end": v(-17.5, 17.5) * mm});
            skPoint(sketch, "E27.middle", {"position": v(0, 0) * mm});
            skSolve(sketch);
        }
        {
            var Q0;
            Q0 = qSketchRegion(id + "F54", true);
            extrude(context, id + "F55", {"entities" : qUnion([Q0]), "operationType" : NewBodyOperationType.ADD, "depth" : 1 * mm});
        }
        {
            var Q0;
            Q0=makeQuery(id+"F55.boolean.opBoolean","MERGE",FACE,{"derivedFrom":[makeQuery(id+"F49.opExtrude","CAP_FACE",FACE,{"disambiguationData":[OSD([sQuery(id+"F48.wireOp",EDGE,"E24.bottom"),sQuery(id+"F48.wireOp",EDGE,"E24.top"),sQuery(id+"F48.wireOp",EDGE,"E24.left"),sQuery(id+"F48.wireOp",EDGE,"E24.right")])],"isStart":false}),makeQuery(id+"F55.opExtrude","CAP_FACE",FACE,{"disambiguationData":[OSD([sQuery(id+"F54.wireOp",EDGE,"E27.bottom"),sQuery(id+"F54.wireOp",EDGE,"E27.top"),sQuery(id+"F54.wireOp",EDGE,"E27.left"),sQuery(id+"F54.wireOp",EDGE,"E27.right")])],"isStart":false})]});
            var sketch = newSketch(context, id + "F56", { "sketchPlane" : qUnion([Q0])});
            skLineSegment(sketch, "E28.bottom", {"start": v(15, -15) * mm, "end": v(-15, -15) * mm});
            skLineSegment(sketch, "E28.top", {"start": v(15, 15) * mm, "end": v(-15, 15) * mm});
            skLineSegment(sketch, "E28.left", {"start": v(15, -15) * mm, "end": v(15, 15) * mm});
            skLineSegment(sketch, "E28.right", {"start": v(-15, -15) * mm, "end": v(-15, 15) * mm});
            skPoint(sketch, "E28.middle", {"position": v(0, 0) * mm});
            skSolve(sketch);
        }
        {
            var Q0;
            Q0 = qSketchRegion(id + "F56", true);
            extrude(context, id + "F57", {"entities" : qUnion([Q0]), "operationType" : NewBodyOperationType.ADD, "depth" : 5 * mm});
        }
        {
            var Q0;
            Q0=makeQuery(id+"F57.opExtrude","CAP_FACE",FACE,{"disambiguationData":[OSD([sQuery(id+"F56.wireOp",EDGE,"E28.bottom"),sQuery(id+"F56.wireOp",EDGE,"E28.top"),sQuery(id+"F56.wireOp",EDGE,"E28.left"),sQuery(id+"F56.wireOp",EDGE,"E28.right")])],"isStart":false});
            var sketch = newSketch(context, id + "F58", { "sketchPlane" : qUnion([Q0])});
            skLineSegment(sketch, "E29.bottom", {"start": v(12.5, -12.5) * mm, "end": v(-12.5, -12.5) * mm});
            skLineSegment(sketch, "E29.top", {"start": v(12.5, 12.5) * mm, "end": v(-12.5, 12.5) * mm});
            skLineSegment(sketch, "E29.left", {"start": v(12.5, -12.5) * mm, "end": v(12.5, 12.5) * mm});
            skLineSegment(sketch, "E29.right", {"start": v(-12.5, -12.5) * mm, "end": v(-12.5, 12.5) * mm});
            skPoint(sketch, "E29.middle", {"position": v(0, 0) * mm});
            skSolve(sketch);
        }
        {
            var Q0;
            Q0 = qSketchRegion(id + "F58", true);
            extrude(context, id + "F59", {"entities" : qUnion([Q0]), "operationType" : NewBodyOperationType.REMOVE, "oppositeDirection" : true, "depth" : 3 * mm});
        }
        {
            var Q0;
            Q0=makeQuery(id+"F59.boolean.opBoolean","COPY",FACE,{"derivedFrom":makeQuery(id+"F59.opExtrude","CAP_FACE",FACE,{"disambiguationData":[OSD([sQuery(id+"F58.wireOp",EDGE,"E29.bottom"),sQuery(id+"F58.wireOp",EDGE,"E29.top"),sQuery(id+"F58.wireOp",EDGE,"E29.left"),sQuery(id+"F58.wireOp",EDGE,"E29.right")])],"isStart":false})});
            var sketch = newSketch(context, id + "F60", { "sketchPlane" : qUnion([Q0])});
            skLineSegment(sketch, "E30.bottom", {"start": v(12.5, -12.5) * mm, "end": v(-12.5, -12.5) * mm});
            skLineSegment(sketch, "E30.top", {"start": v(12.5, 12.5) * mm, "end": v(-12.5, 12.5) * mm});
            skLineSegment(sketch, "E30.left", {"start": v(12.5, -12.5) * mm, "end": v(12.5, 12.5) * mm});
            skLineSegment(sketch, "E30.right", {"start": v(-12.5, -12.5) * mm, "end": v(-12.5, 12.5) * mm});
            skPoint(sketch, "E30.middle", {"position": v(0, 0) * mm});
            skSolve(sketch);
        }
        {
            var Q0;
            Q0 = qSketchRegion(id + "F60", true);
            extrude(context, id + "F61", {"entities" : qUnion([Q0]), "depth" : 2 * mm});
        }
        {
            var Q0;
            Q0=makeQuery(id+"F61.opExtrude","CAP_FACE",FACE,{"disambiguationData":[OSD([sQuery(id+"F60.wireOp",EDGE,"E30.bottom"),sQuery(id+"F60.wireOp",EDGE,"E30.top"),sQuery(id+"F60.wireOp",EDGE,"E30.left"),sQuery(id+"F60.wireOp",EDGE,"E30.right")])],"isStart":false});
            var sketch = newSketch(context, id + "F62", { "sketchPlane" : qUnion([Q0])});
            skLineSegment(sketch, "E31.bottom", {"start": v(12.5, -12.5) * mm, "end": v(-12.5, -12.5) * mm});
            skLineSegment(sketch, "E31.top", {"start": v(12.5, 12.5) * mm, "end": v(-12.5, 12.5) * mm});
            skLineSegment(sketch, "E31.left", {"start": v(12.5, -12.5) * mm, "end": v(12.5, 12.5) * mm});
            skLineSegment(sketch, "E31.right", {"start": v(-12.5, -12.5) * mm, "end": v(-12.5, 12.5) * mm});
            skPoint(sketch, "E31.middle", {"position": v(0, 0) * mm});
            skSolve(sketch);
        }
        {
            var Q0;
            Q0 = qSketchRegion(id + "F62", true);
            extrude(context, id + "F63", {"entities" : qUnion([Q0]), "operationType" : NewBodyOperationType.ADD, "depth" : 1 * mm});
        }
        {
            var Q0;
            Q0=makeQuery(id+"F63.boolean.opBoolean","MERGE",FACE,{"derivedFrom":[makeQuery(id+"F57.opExtrude","CAP_FACE",FACE,{"disambiguationData":[OSD([sQuery(id+"F56.wireOp",EDGE,"E28.bottom"),sQuery(id+"F56.wireOp",EDGE,"E28.top"),sQuery(id+"F56.wireOp",EDGE,"E28.left"),sQuery(id+"F56.wireOp",EDGE,"E28.right")])],"isStart":false}),makeQuery(id+"F63.opExtrude","CAP_FACE",FACE,{"disambiguationData":[OSD([sQuery(id+"F62.wireOp",EDGE,"E31.bottom"),sQuery(id+"F62.wireOp",EDGE,"E31.top"),sQuery(id+"F62.wireOp",EDGE,"E31.left"),sQuery(id+"F62.wireOp",EDGE,"E31.right")])],"isStart":false})]});
            var sketch = newSketch(context, id + "F64", { "sketchPlane" : qUnion([Q0])});
            skLineSegment(sketch, "E32.bottom", {"start": v(10, -10) * mm, "end": v(-10, -10) * mm});
            skLineSegment(sketch, "E32.top", {"start": v(10, 10) * mm, "end": v(-10, 10) * mm});
            skLineSegment(sketch, "E32.left", {"start": v(10, -10) * mm, "end": v(10, 10) * mm});
            skLineSegment(sketch, "E32.right", {"start": v(-10, -10) * mm, "end": v(-10, 10) * mm});
            skPoint(sketch, "E32.middle", {"position": v(0, 0) * mm});
            skSolve(sketch);
        }
        {
            var Q0;
            Q0 = qSketchRegion(id + "F64", true);
            extrude(context, id + "F65", {"entities" : qUnion([Q0]), "operationType" : NewBodyOperationType.ADD, "depth" : 5 * mm});
        }
        {
            var Q0;
            Q0=makeQuery(id+"F65.opExtrude","CAP_FACE",FACE,{"disambiguationData":[OSD([sQuery(id+"F64.wireOp",EDGE,"E32.bottom"),sQuery(id+"F64.wireOp",EDGE,"E32.top"),sQuery(id+"F64.wireOp",EDGE,"E32.left"),sQuery(id+"F64.wireOp",EDGE,"E32.right")])],"isStart":false});
            var sketch = newSketch(context, id + "F66", { "sketchPlane" : qUnion([Q0])});
            skLineSegment(sketch, "E33.bottom", {"start": v(7.5, -7.5) * mm, "end": v(-7.5, -7.5) * mm});
            skLineSegment(sketch, "E33.top", {"start": v(7.5, 7.5) * mm, "end": v(-7.5, 7.5) * mm});
            skLineSegment(sketch, "E33.left", {"start": v(7.5, -7.5) * mm, "end": v(7.5, 7.5) * mm});
            skLineSegment(sketch, "E33.right", {"start": v(-7.5, -7.5) * mm, "end": v(-7.5, 7.5) * mm});
            skPoint(sketch, "E33.middle", {"position": v(0, 0) * mm});
            skSolve(sketch);
        }
        {
            var Q0;
            Q0 = qSketchRegion(id + "F66", true);
            extrude(context, id + "F67", {"entities" : qUnion([Q0]), "operationType" : NewBodyOperationType.REMOVE, "oppositeDirection" : true, "depth" : 3 * mm});
        }
        {
            var Q0;
            Q0=makeQuery(id+"F67.boolean.opBoolean","COPY",FACE,{"derivedFrom":makeQuery(id+"F67.opExtrude","CAP_FACE",FACE,{"disambiguationData":[OSD([sQuery(id+"F66.wireOp",EDGE,"E33.bottom"),sQuery(id+"F66.wireOp",EDGE,"E33.top"),sQuery(id+"F66.wireOp",EDGE,"E33.left"),sQuery(id+"F66.wireOp",EDGE,"E33.right")])],"isStart":false})});
            var sketch = newSketch(context, id + "F68", { "sketchPlane" : qUnion([Q0])});
            skLineSegment(sketch, "E34.bottom", {"start": v(7.5, -7.5) * mm, "end": v(-7.5, -7.5) * mm});
            skLineSegment(sketch, "E34.top", {"start": v(7.5, 7.5) * mm, "end": v(-7.5, 7.5) * mm});
            skLineSegment(sketch, "E34.left", {"start": v(7.5, -7.5) * mm, "end": v(7.5, 7.5) * mm});
            skLineSegment(sketch, "E34.right", {"start": v(-7.5, -7.5) * mm, "end": v(-7.5, 7.5) * mm});
            skPoint(sketch, "E34.middle", {"position": v(0, 0) * mm});
            skSolve(sketch);
        }
        {
            var Q0;
            Q0 = qSketchRegion(id + "F68", true);
            extrude(context, id + "F69", {"entities" : qUnion([Q0]), "depth" : 2 * mm});
        }
        {
            var Q0;
            Q0=makeQuery(id+"F69.opExtrude","CAP_FACE",FACE,{"disambiguationData":[OSD([sQuery(id+"F68.wireOp",EDGE,"E34.bottom"),sQuery(id+"F68.wireOp",EDGE,"E34.top"),sQuery(id+"F68.wireOp",EDGE,"E34.left"),sQuery(id+"F68.wireOp",EDGE,"E34.right")])],"isStart":false});
            var sketch = newSketch(context, id + "F70", { "sketchPlane" : qUnion([Q0])});
            skLineSegment(sketch, "E35.bottom", {"start": v(7.5, -7.5) * mm, "end": v(-7.5, -7.5) * mm});
            skLineSegment(sketch, "E35.top", {"start": v(7.5, 7.5) * mm, "end": v(-7.5, 7.5) * mm});
            skLineSegment(sketch, "E35.left", {"start": v(7.5, -7.5) * mm, "end": v(7.5, 7.5) * mm});
            skLineSegment(sketch, "E35.right", {"start": v(-7.5, -7.5) * mm, "end": v(-7.5, 7.5) * mm});
            skPoint(sketch, "E35.middle", {"position": v(0, 0) * mm});
            skSolve(sketch);
        }
        {
            var Q0;
            Q0 = qSketchRegion(id + "F70", true);
            extrude(context, id + "F71", {"entities" : qUnion([Q0]), "operationType" : NewBodyOperationType.ADD, "depth" : 1 * mm});
        }
        {
            var Q0;
            Q0=makeQuery(id+"F71.boolean.opBoolean","MERGE",FACE,{"derivedFrom":[makeQuery(id+"F65.opExtrude","CAP_FACE",FACE,{"disambiguationData":[OSD([sQuery(id+"F64.wireOp",EDGE,"E32.bottom"),sQuery(id+"F64.wireOp",EDGE,"E32.top"),sQuery(id+"F64.wireOp",EDGE,"E32.left"),sQuery(id+"F64.wireOp",EDGE,"E32.right")])],"isStart":false}),makeQuery(id+"F71.opExtrude","CAP_FACE",FACE,{"disambiguationData":[OSD([sQuery(id+"F70.wireOp",EDGE,"E35.bottom"),sQuery(id+"F70.wireOp",EDGE,"E35.top"),sQuery(id+"F70.wireOp",EDGE,"E35.left"),sQuery(id+"F70.wireOp",EDGE,"E35.right")])],"isStart":false})]});
            var sketch = newSketch(context, id + "F72", { "sketchPlane" : qUnion([Q0])});
            skLineSegment(sketch, "E36.bottom", {"start": v(5, -5) * mm, "end": v(-5, -5) * mm});
            skLineSegment(sketch, "E36.top", {"start": v(5, 5) * mm, "end": v(-5, 5) * mm});
            skLineSegment(sketch, "E36.left", {"start": v(5, -5) * mm, "end": v(5, 5) * mm});
            skLineSegment(sketch, "E36.right", {"start": v(-5, -5) * mm, "end": v(-5, 5) * mm});
            skPoint(sketch, "E36.middle", {"position": v(0, 0) * mm});
            skSolve(sketch);
        }
        {
            var Q0;
            Q0 = qSketchRegion(id + "F72", true);
            extrude(context, id + "F73", {"entities" : qUnion([Q0]), "operationType" : NewBodyOperationType.ADD, "depth" : 5 * mm});
        }
        {
            var Q0;
            Q0=makeQuery(id+"F73.opExtrude","CAP_FACE",FACE,{"disambiguationData":[OSD([sQuery(id+"F72.wireOp",EDGE,"E36.bottom"),sQuery(id+"F72.wireOp",EDGE,"E36.top"),sQuery(id+"F72.wireOp",EDGE,"E36.left"),sQuery(id+"F72.wireOp",EDGE,"E36.right")])],"isStart":false});
            var sketch = newSketch(context, id + "F74", { "sketchPlane" : qUnion([Q0])});
            skLineSegment(sketch, "E37.bottom", {"start": v(2.5, -2.5) * mm, "end": v(-2.5, -2.5) * mm});
            skLineSegment(sketch, "E37.top", {"start": v(2.5, 2.5) * mm, "end": v(-2.5, 2.5) * mm});
            skLineSegment(sketch, "E37.left", {"start": v(2.5, -2.5) * mm, "end": v(2.5, 2.5) * mm});
            skLineSegment(sketch, "E37.right", {"start": v(-2.5, -2.5) * mm, "end": v(-2.5, 2.5) * mm});
            skPoint(sketch, "E37.middle", {"position": v(0, 0) * mm});
            skSolve(sketch);
        }
        {
            var Q0;
            Q0 = qSketchRegion(id + "F74", true);
            extrude(context, id + "F75", {"entities" : qUnion([Q0]), "operationType" : NewBodyOperationType.REMOVE, "oppositeDirection" : true, "depth" : 3 * mm});
        }
        {
            var Q0;
            Q0=makeQuery(id+"F75.boolean.opBoolean","COPY",FACE,{"derivedFrom":makeQuery(id+"F75.opExtrude","CAP_FACE",FACE,{"disambiguationData":[OSD([sQuery(id+"F74.wireOp",EDGE,"E37.bottom"),sQuery(id+"F74.wireOp",EDGE,"E37.top"),sQuery(id+"F74.wireOp",EDGE,"E37.left"),sQuery(id+"F74.wireOp",EDGE,"E37.right")])],"isStart":false})});
            var sketch = newSketch(context, id + "F76", { "sketchPlane" : qUnion([Q0])});
            skLineSegment(sketch, "E38.bottom", {"start": v(2.5, -2.5) * mm, "end": v(-2.5, -2.5) * mm});
            skLineSegment(sketch, "E38.top", {"start": v(2.5, 2.5) * mm, "end": v(-2.5, 2.5) * mm});
            skLineSegment(sketch, "E38.left", {"start": v(2.5, -2.5) * mm, "end": v(2.5, 2.5) * mm});
            skLineSegment(sketch, "E38.right", {"start": v(-2.5, -2.5) * mm, "end": v(-2.5, 2.5) * mm});
            skPoint(sketch, "E38.middle", {"position": v(0, 0) * mm});
            skSolve(sketch);
        }
        {
            var Q0;
            Q0 = qSketchRegion(id + "F76", true);
            extrude(context, id + "F77", {"entities" : qUnion([Q0]), "depth" : 2 * mm});
        }
        {
            var Q0;
            Q0=makeQuery(id+"F77.opExtrude","CAP_FACE",FACE,{"disambiguationData":[OSD([sQuery(id+"F76.wireOp",EDGE,"E38.bottom"),sQuery(id+"F76.wireOp",EDGE,"E38.top"),sQuery(id+"F76.wireOp",EDGE,"E38.left"),sQuery(id+"F76.wireOp",EDGE,"E38.right")])],"isStart":false});
            var sketch = newSketch(context, id + "F78", { "sketchPlane" : qUnion([Q0])});
            skLineSegment(sketch, "E39.bottom", {"start": v(2.5, -2.5) * mm, "end": v(-2.5, -2.5) * mm});
            skLineSegment(sketch, "E39.top", {"start": v(2.5, 2.5) * mm, "end": v(-2.5, 2.5) * mm});
            skLineSegment(sketch, "E39.left", {"start": v(2.5, -2.5) * mm, "end": v(2.5, 2.5) * mm});
            skLineSegment(sketch, "E39.right", {"start": v(-2.5, -2.5) * mm, "end": v(-2.5, 2.5) * mm});
            skPoint(sketch, "E39.middle", {"position": v(0, 0) * mm});
            skSolve(sketch);
        }
        {
            var Q0;
            Q0 = qSketchRegion(id + "F78", true);
            extrude(context, id + "F79", {"entities" : qUnion([Q0]), "operationType" : NewBodyOperationType.ADD, "depth" : 1 * mm});
        }
    });
